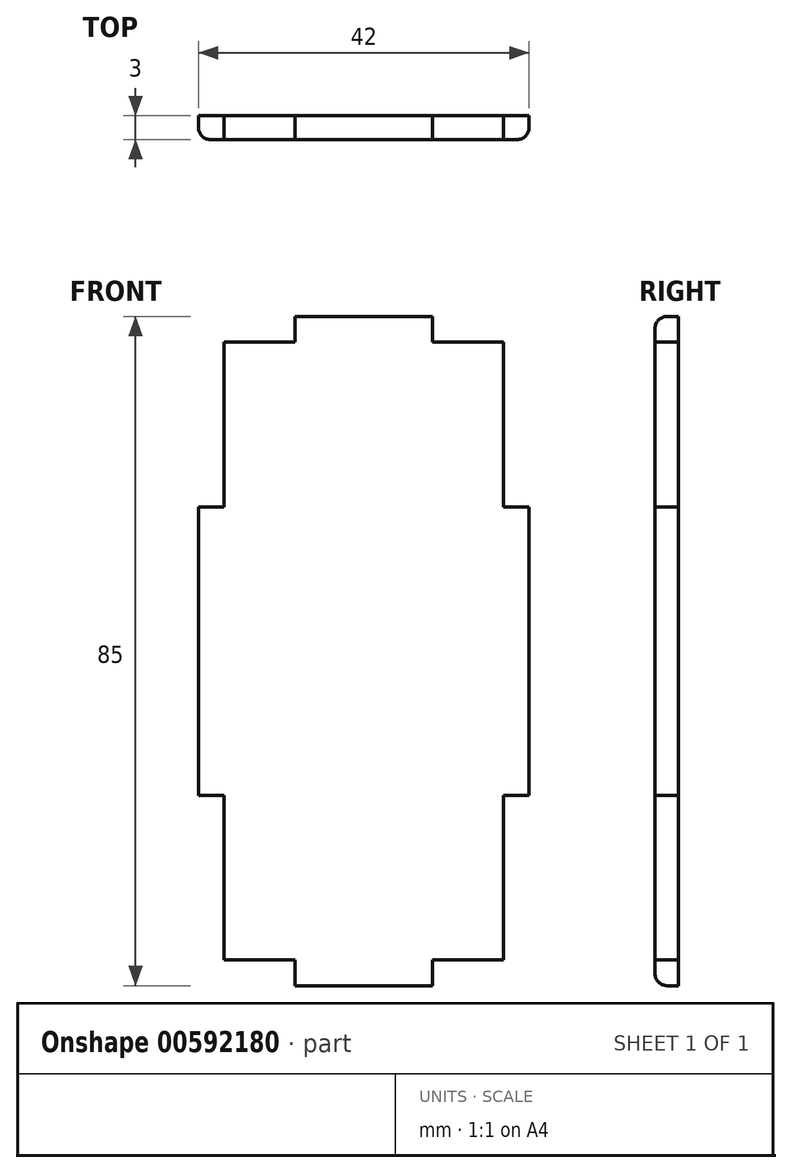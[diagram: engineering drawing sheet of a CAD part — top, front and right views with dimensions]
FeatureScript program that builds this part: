
annotation { "Feature Type Name" : "Feature", "Feature Type Description" : "" }
export const myFeature = defineFeature(function(context is Context, id is Id, definition is map)
    precondition{}
    {
        {
            var Q0;
            Q0=qCreatedBy(makeId("Front.planeOp"),FACE);
            var sketch = newSketch(context, id + "F0", { "sketchPlane" : qUnion([Q0])});
            skLineSegment(sketch, "E0.bottom", {"start": v(-33.3, 32.93) * mm, "end": v(8.7, 32.93) * mm});
            skLineSegment(sketch, "E0.top", {"start": v(-33.3, -52.07) * mm, "end": v(8.7, -52.07) * mm});
            skLineSegment(sketch, "E0.left", {"start": v(-33.3, 32.93) * mm, "end": v(-33.3, -52.07) * mm});
            skLineSegment(sketch, "E0.right", {"start": v(8.7, 32.93) * mm, "end": v(8.7, -52.07) * mm});
            skSolve(sketch);
        }
        {
            var Q0;
            Q0 = qSketchRegion(id + "F0", true);
            extrude(context, id + "F1", {"entities" : qUnion([Q0]), "depth" : 3 * mm, "offsetDistance" : 25 * mm});
        }
        {
            var Q0;
            Q0=makeQuery(id+"F1.opExtrude","SWEPT_EDGE",EDGE,{"disambiguationData":[OSD([sQuery(id+"F0.wireOp",EDGE,"E0.bottom"),sQuery(id+"F0.wireOp",EDGE,"E0.left")])]});
            var Q1;
            Q1=makeQuery(id+"F1.opExtrude","SWEPT_EDGE",EDGE,{"disambiguationData":[OSD([sQuery(id+"F0.wireOp",EDGE,"E0.bottom"),sQuery(id+"F0.wireOp",EDGE,"E0.right")])]});
            var Q2;
            Q2=makeQuery(id+"F1.opExtrude","SWEPT_EDGE",EDGE,{"disambiguationData":[OSD([sQuery(id+"F0.wireOp",EDGE,"E0.top"),sQuery(id+"F0.wireOp",EDGE,"E0.right")])]});
            var Q3;
            Q3=makeQuery(id+"F1.opExtrude","SWEPT_EDGE",EDGE,{"disambiguationData":[OSD([sQuery(id+"F0.wireOp",EDGE,"E0.top"),sQuery(id+"F0.wireOp",EDGE,"E0.left")])]});
            fillet(context, id + "F2", {"entities" : qUnion([Q0, Q1, Q2, Q3]), "tangentPropagation" : true, "radius" : 3 * mm, "defaultsChanged" : false, "vertexSettings" : [], "allowEdgeOverflow" : false});
        }
        {
            var Q0;
            Q0=makeQuery(id+"F1.opExtrude","CAP_FACE",FACE,{"disambiguationData":[OSD([sQuery(id+"F0.wireOp",EDGE,"E0.bottom"),sQuery(id+"F0.wireOp",EDGE,"E0.top"),sQuery(id+"F0.wireOp",EDGE,"E0.left"),sQuery(id+"F0.wireOp",EDGE,"E0.right")])],"isStart":true});
            var sketch = newSketch(context, id + "F3", { "sketchPlane" : qUnion([Q0])});
            skLineSegment(sketch, "E1.bottom", {"start": v(-5.46, 29.68) * mm, "end": v(30.04, 29.68) * mm});
            skLineSegment(sketch, "E1.top", {"start": v(-5.46, -48.82) * mm, "end": v(30.04, -48.82) * mm});
            skLineSegment(sketch, "E1.left", {"start": v(-5.46, 29.68) * mm, "end": v(-5.46, -48.82) * mm});
            skLineSegment(sketch, "E1.right", {"start": v(30.04, 29.68) * mm, "end": v(30.04, -48.82) * mm});
            skLineSegment(sketch, "E2", {"start": v(3.54, 32.93) * mm, "end": v(3.54, 29.68) * mm});
            skPoint(sketch, "E2.endSnap0", {"position": v(12.3, 29.68) * mm});
            skLineSegment(sketch, "E3", {"start": v(3.54, 29.68) * mm, "end": v(21.04, 29.68) * mm});
            skLineSegment(sketch, "E4", {"start": v(21.04, 29.68) * mm, "end": v(21.04, 32.93) * mm});
            skLineSegment(sketch, "E5", {"start": v(21.04, 32.93) * mm, "end": v(3.54, 32.93) * mm});
            skLineSegment(sketch, "E6", {"start": v(3.54, -48.82) * mm, "end": v(3.54, -52.07) * mm});
            skLineSegment(sketch, "E7", {"start": v(3.54, -52.07) * mm, "end": v(21.04, -52.07) * mm});
            skLineSegment(sketch, "E8", {"start": v(21.04, -52.07) * mm, "end": v(21.04, -48.82) * mm});
            skLineSegment(sketch, "E9", {"start": v(21.04, -48.82) * mm, "end": v(3.54, -48.82) * mm});
            skLineSegment(sketch, "E10", {"start": v(-8.7, 8.76) * mm, "end": v(-5.46, 8.76) * mm});
            skLineSegment(sketch, "E11", {"start": v(-5.46, 8.76) * mm, "end": v(-5.46, -27.9) * mm});
            skLineSegment(sketch, "E12", {"start": v(-5.46, -27.9) * mm, "end": v(-8.7, -27.9) * mm});
            skLineSegment(sketch, "E13", {"start": v(-8.7, -27.9) * mm, "end": v(-8.7, 8.76) * mm});
            skLineSegment(sketch, "E14", {"start": v(30.04, 8.76) * mm, "end": v(33.3, 8.76) * mm});
            skLineSegment(sketch, "E15", {"start": v(33.3, 8.76) * mm, "end": v(33.3, -27.9) * mm});
            skLineSegment(sketch, "E16", {"start": v(33.3, -27.9) * mm, "end": v(30.04, -27.9) * mm});
            skLineSegment(sketch, "E17", {"start": v(30.04, -27.9) * mm, "end": v(30.04, 8.76) * mm});
            skSolve(sketch);
        }
        {
            var Q0;
            {var subQ1=sQuery(id+"F3.wireOp",EDGE,"E2");Q0=makeQuery(id+"F3.imprint","IMPRINT",FACE,{"disambiguationData":[TD([[makeQuery(id+"F3.imprint","IMPRINT",EDGE,{"derivedFrom":subQ1}),-1.0]])]});}
            var Q1;
            {var subQ1=sQuery(id+"F3.wireOp",EDGE,"E4");Q1=makeQuery(id+"F3.imprint","IMPRINT",FACE,{"disambiguationData":[TD([[makeQuery(id+"F3.imprint","IMPRINT",EDGE,{"derivedFrom":subQ1}),-1.0]])]});}
            var Q2;
            {var subQ0=sQuery(id+"F3.wireOp",EDGE,"E8");Q2=makeQuery(id+"F3.imprint","IMPRINT",FACE,{"disambiguationData":[TD([[makeQuery(id+"F3.imprint","IMPRINT",EDGE,{"derivedFrom":subQ0}),-1.0]])]});}
            var Q3;
            {var subQ7=sQuery(id+"F3.wireOp",EDGE,"E6");Q3=makeQuery(id+"F3.imprint","IMPRINT",FACE,{"disambiguationData":[TD([[makeQuery(id+"F3.imprint","IMPRINT",EDGE,{"derivedFrom":subQ7}),-1.0]])]});}
            extrude(context, id + "F4", {"entities" : qUnion([Q0, Q1, Q2, Q3]), "operationType" : NewBodyOperationType.REMOVE, "endBound" : BoundingType.UP_TO_NEXT, "oppositeDirection" : true, "depth" : 25 * mm, "offsetDistance" : 25 * mm});
        }
        {
            var Q0;
            Q0=makeQuery(id+"F1.opExtrude","CAP_EDGE",EDGE,{"disambiguationData":[OSD([sQuery(id+"F0.wireOp",EDGE,"E0.bottom")])],"isStart":false});
            var Q1;
            Q1=makeQuery(id+"F1.opExtrude","CAP_EDGE",EDGE,{"disambiguationData":[OSD([sQuery(id+"F0.wireOp",EDGE,"E0.right")])],"isStart":false});
            var Q2;
            Q2=makeQuery(id+"F1.opExtrude","CAP_EDGE",EDGE,{"disambiguationData":[OSD([sQuery(id+"F0.wireOp",EDGE,"E0.top")])],"isStart":false});
            var Q3;
            Q3=makeQuery(id+"F1.opExtrude","CAP_EDGE",EDGE,{"disambiguationData":[OSD([sQuery(id+"F0.wireOp",EDGE,"E0.left")])],"isStart":false});
            fillet(context, id + "F5", {"entities" : qUnion([Q0, Q1, Q2, Q3]), "tangentPropagation" : true, "radius" : 1.5 * mm, "defaultsChanged" : false, "vertexSettings" : [], "allowEdgeOverflow" : false});
        }
    });
